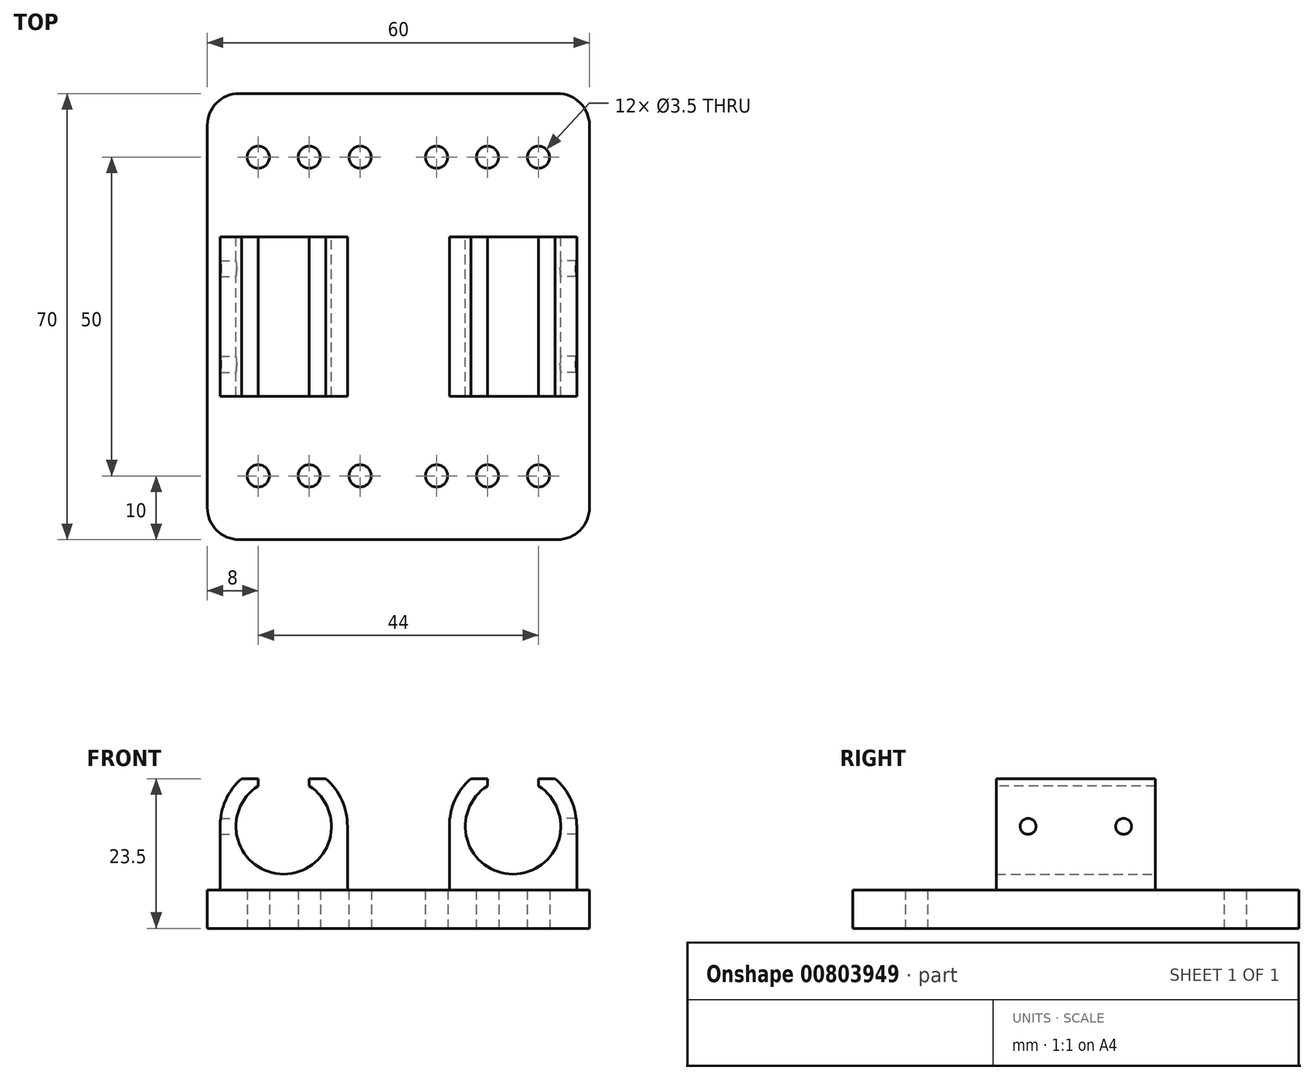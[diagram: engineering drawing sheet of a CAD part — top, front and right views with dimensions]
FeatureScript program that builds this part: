
annotation { "Feature Type Name" : "Feature", "Feature Type Description" : "" }
export const myFeature = defineFeature(function(context is Context, id is Id, definition is map)
    precondition{}
    {
        {
            var Q0;
            Q0=qCreatedBy(makeId("Top.planeOp"),FACE);
            var sketch = newSketch(context, id + "F0", { "sketchPlane" : qUnion([Q0])});
            skLineSegment(sketch, "E0.bottom", {"start": v(30, 35) * mm, "end": v(-30, 35) * mm});
            skLineSegment(sketch, "E0.top", {"start": v(30, -35) * mm, "end": v(-30, -35) * mm});
            skLineSegment(sketch, "E0.left", {"start": v(30, 35) * mm, "end": v(30, -35) * mm});
            skLineSegment(sketch, "E0.right", {"start": v(-30, 35) * mm, "end": v(-30, -35) * mm});
            skPoint(sketch, "E0.middle", {"position": v(0, 0) * mm});
            skLineSegment(sketch, "E1.bottom", {"start": v(-28, 12.5) * mm, "end": v(-8, 12.5) * mm});
            skLineSegment(sketch, "E1.top", {"start": v(-28, -12.5) * mm, "end": v(-8, -12.5) * mm});
            skLineSegment(sketch, "E1.left", {"start": v(-28, 12.5) * mm, "end": v(-28, -12.5) * mm});
            skLineSegment(sketch, "E1.right", {"start": v(-8, 12.5) * mm, "end": v(-8, -12.5) * mm});
            skPoint(sketch, "E1.middle", {"position": v(-18, 0) * mm});
            skLineSegment(sketch, "E2.bottom", {"start": v(8, 12.5) * mm, "end": v(28, 12.5) * mm});
            skLineSegment(sketch, "E2.top", {"start": v(8, -12.5) * mm, "end": v(28, -12.5) * mm});
            skLineSegment(sketch, "E2.left", {"start": v(8, 12.5) * mm, "end": v(8, -12.5) * mm});
            skLineSegment(sketch, "E2.right", {"start": v(28, 12.5) * mm, "end": v(28, -12.5) * mm});
            skPoint(sketch, "E2.middle", {"position": v(18, 0) * mm});
            skLineSegment(sketch, "E3", {"start": v(-30, -25) * mm, "end": v(30, -25) * mm});
            skPoint(sketch, "E4", {"position": v(22, -25) * mm});
            skPoint(sketch, "E5", {"position": v(6, -25) * mm});
            skPoint(sketch, "E6", {"position": v(-6, -25) * mm});
            skPoint(sketch, "E7", {"position": v(-22, -25) * mm});
            skPoint(sketch, "E8", {"position": v(-14, -25) * mm});
            skPoint(sketch, "E9", {"position": v(14, -25) * mm});
            skLineSegment(sketch, "E10", {"start": v(-30, 25) * mm, "end": v(30, 25) * mm});
            skPoint(sketch, "E11", {"position": v(-22, 25) * mm});
            skPoint(sketch, "E12", {"position": v(-14, 25) * mm});
            skPoint(sketch, "E13", {"position": v(-6, 25) * mm});
            skPoint(sketch, "E14", {"position": v(22, 25) * mm});
            skPoint(sketch, "E15", {"position": v(14, 25) * mm});
            skPoint(sketch, "E16", {"position": v(6, 25) * mm});
            skSolve(sketch);
        }
        {
            var Q0;
            Q0=makeQuery(id+"F0.imprint","IMPRINT",FACE,{"disambiguationData":[TD([[makeQuery(id+"F0.imprint","IMPRINT",EDGE,{"derivedFrom":sQuery(id+"F0.wireOp",EDGE,"E0.bottom")}),1.0]])]});
            var Q1;
            Q1=makeQuery(id+"F0.imprint","IMPRINT",FACE,{"disambiguationData":[TD([[makeQuery(id+"F0.imprint","IMPRINT",EDGE,{"derivedFrom":sQuery(id+"F0.wireOp",EDGE,"E1.bottom")}),-1.0]])]});
            var Q2;
            Q2=makeQuery(id+"F0.imprint","IMPRINT",FACE,{"disambiguationData":[TD([[makeQuery(id+"F0.imprint","IMPRINT",EDGE,{"derivedFrom":sQuery(id+"F0.wireOp",EDGE,"E2.bottom")}),-1.0]])]});
            var Q3;
            Q3=makeQuery(id+"F0.imprint","IMPRINT",FACE,{"disambiguationData":[TD([[makeQuery(id+"F0.imprint","IMPRINT",EDGE,{"derivedFrom":sQuery(id+"F0.wireOp",EDGE,"E1.bottom")}),1.0]])]});
            var Q4;
            {var subQ0=sQuery(id+"F0.wireOp",EDGE,"E0.top");Q4=makeQuery(id+"F0.imprint","IMPRINT",FACE,{"disambiguationData":[TD([[makeQuery(id+"F0.imprint","IMPRINT",EDGE,{"derivedFrom":subQ0}),-1.0]])]});}
            extrude(context, id + "F1", {"entities" : qUnion([Q0, Q1, Q2, Q3, Q4]), "oppositeDirection" : true, "depth" : 6 * mm, "offsetDistance" : 25 * mm});
        }
        {
            var Q0;
            Q0=makeQuery(id+"F0.imprint","IMPRINT",FACE,{"disambiguationData":[TD([[makeQuery(id+"F0.imprint","IMPRINT",EDGE,{"derivedFrom":sQuery(id+"F0.wireOp",EDGE,"E1.bottom")}),-1.0]])]});
            var Q1;
            Q1=makeQuery(id+"F0.imprint","IMPRINT",FACE,{"disambiguationData":[TD([[makeQuery(id+"F0.imprint","IMPRINT",EDGE,{"derivedFrom":sQuery(id+"F0.wireOp",EDGE,"E2.bottom")}),-1.0]])]});
            extrude(context, id + "F2", {"entities" : qUnion([Q0, Q1]), "operationType" : NewBodyOperationType.ADD, "depth" : 10 * mm, "offsetDistance" : 25 * mm});
        }
        {
            var Q0;
            Q0=makeQuery(id+"F2.opExtrude","SWEPT_FACE",FACE,{"disambiguationData":[OSD([sQuery(id+"F0.wireOp",EDGE,"E1.top")])]});
            var sketch = newSketch(context, id + "F3", { "sketchPlane" : qUnion([Q0])});
            skCircle(sketch, "E17", {"center": v(-18, 10) * mm, "radius": 10 * mm});
            skCircle(sketch, "E18", {"center": v(-18, 10) * mm, "radius": 7.5 * mm});
            skLineSegment(sketch, "E19.bottom", {"start": v(-11.39, 17.5) * mm, "end": v(-24.61, 17.5) * mm});
            skLineSegment(sketch, "E19.top", {"start": v(-11.39, 2.5) * mm, "end": v(-24.61, 2.5) * mm});
            skLineSegment(sketch, "E19.left", {"start": v(-11.39, 17.5) * mm, "end": v(-11.39, 2.5) * mm});
            skLineSegment(sketch, "E19.right", {"start": v(-24.61, 17.5) * mm, "end": v(-24.61, 2.5) * mm});
            skLineSegment(sketch, "E20.bottom", {"start": v(-22, 21.5) * mm, "end": v(-14, 21.5) * mm});
            skLineSegment(sketch, "E20.top", {"start": v(-22, 13.5) * mm, "end": v(-14, 13.5) * mm});
            skLineSegment(sketch, "E20.left", {"start": v(-22, 21.5) * mm, "end": v(-22, 13.5) * mm});
            skLineSegment(sketch, "E20.right", {"start": v(-14, 21.5) * mm, "end": v(-14, 13.5) * mm});
            skPoint(sketch, "E20.middle", {"position": v(-18, 17.5) * mm});
            skPoint(sketch, "E21", {"position": v(18, 10) * mm});
            skCircle(sketch, "E22", {"center": v(18, 10) * mm, "radius": 7.5 * mm});
            skSolve(sketch);
        }
        {
            var Q0;
            {var subQ4=sQuery(id+"F3.wireOp",EDGE,"E19.right");var subQ6=sQuery(id+"F3.wireOp",EDGE,"E18");var subQ7=makeQuery(id+"F3.imprint","INTERSECT",VERTEX,{"disambiguationData":[OD(0.0)],"derivedFrom":[subQ6,subQ4]});Q0=makeQuery(id+"F3.imprint","IMPRINT",FACE,{"disambiguationData":[TD([[makeQuery(id+"F3.imprint","IMPRINT",EDGE,{"disambiguationData":[TD([[subQ7,-1.0]])],"derivedFrom":subQ6}),-1.0]])]});}
            var Q1;
            {var subQ0=sQuery(id+"F3.wireOp",EDGE,"E20.left");var subQ1=sQuery(id+"F3.wireOp",EDGE,"E18");var subQ2=makeQuery(id+"F3.imprint","INTERSECT",VERTEX,{"derivedFrom":[subQ1,subQ0]});Q1=makeQuery(id+"F3.imprint","IMPRINT",FACE,{"disambiguationData":[TD([[makeQuery(id+"F3.imprint","IMPRINT",EDGE,{"disambiguationData":[TD([[subQ2,-1.0]])],"derivedFrom":subQ1}),-1.0]])]});}
            var Q2;
            {var subQ0=sQuery(id+"F3.wireOp",EDGE,"E19.left");var subQ1=sQuery(id+"F3.wireOp",EDGE,"E18");var subQ2=makeQuery(id+"F3.imprint","INTERSECT",VERTEX,{"disambiguationData":[OD(0.0)],"derivedFrom":[subQ1,subQ0]});Q2=makeQuery(id+"F3.imprint","IMPRINT",FACE,{"disambiguationData":[TD([[makeQuery(id+"F3.imprint","IMPRINT",EDGE,{"disambiguationData":[TD([[subQ2,-1.0]])],"derivedFrom":subQ1}),-1.0]])]});}
            var Q3;
            {var subQ4=sQuery(id+"F3.wireOp",EDGE,"E19.left");var subQ6=sQuery(id+"F3.wireOp",EDGE,"E18");var subQ7=makeQuery(id+"F3.imprint","INTERSECT",VERTEX,{"disambiguationData":[OD(0.0)],"derivedFrom":[subQ6,subQ4]});Q3=makeQuery(id+"F3.imprint","IMPRINT",FACE,{"disambiguationData":[TD([[makeQuery(id+"F3.imprint","IMPRINT",EDGE,{"disambiguationData":[TD([[subQ7,1.0]])],"derivedFrom":subQ6}),-1.0]])]});}
            extrude(context, id + "F4", {"entities" : qUnion([Q0, Q1, Q2, Q3]), "oppositeDirection" : true, "depth" : 25 * mm, "offsetDistance" : 25 * mm});
        }
        {
            var Q0;
            Q0=sQuery(id+"F3.wireOp",VERTEX,"E17.center");
            var Q1;
            Q1=makeQuery(id+"F1.opExtrude","SWEPT_BODY",BODY,{"disambiguationData":[OSD([sQuery(id+"F0.wireOp",EDGE,"E0.bottom"),sQuery(id+"F0.wireOp",EDGE,"E0.top"),sQuery(id+"F0.wireOp",EDGE,"E0.left"),sQuery(id+"F0.wireOp",EDGE,"E0.right")])]});
            hole(context, id + "F5", {"style" : HoleStyle.SIMPLE, "endStyle" : HoleEndStyle.THROUGH, "holeDiameter" : 15 * mm, "majorDiameter" : 5 * mm, "isTappedThrough" : true, "tappedDepth" : 12 * mm, "tapClearance" : 3, "locations" : qUnion([Q0]), "scope" : qUnion([Q1])});
        }
        {
            var Q0;
            Q0=makeQuery(id+"F1.opExtrude","SWEPT_BODY",BODY,{"disambiguationData":[OSD([sQuery(id+"F0.wireOp",EDGE,"E0.bottom"),sQuery(id+"F0.wireOp",EDGE,"E0.top"),sQuery(id+"F0.wireOp",EDGE,"E0.left"),sQuery(id+"F0.wireOp",EDGE,"E0.right")])]});
            var Q1;
            Q1=makeQuery(id+"F4.opExtrude","SWEPT_BODY",BODY,{"disambiguationData":[OSD([sQuery(id+"F0.wireOp",EDGE,"E1.top"),sQuery(id+"F3.wireOp",EDGE,"E17"),sQuery(id+"F3.wireOp",EDGE,"E18"),sQuery(id+"F3.wireOp",EDGE,"E19.bottom"),sQuery(id+"F3.wireOp",EDGE,"E20.right")])]});
            var Q2;
            Q2=makeQuery(id+"F4.opExtrude","SWEPT_BODY",BODY,{"disambiguationData":[OSD([sQuery(id+"F0.wireOp",EDGE,"E1.top"),sQuery(id+"F3.wireOp",EDGE,"E17"),sQuery(id+"F3.wireOp",EDGE,"E18"),sQuery(id+"F3.wireOp",EDGE,"E19.bottom"),sQuery(id+"F3.wireOp",EDGE,"E20.left")])]});
            booleanBodies(context, id + "F6", {"operationType" : BooleanOperationType.UNION, "tools" : qUnion([Q0, Q1, Q2])});
        }
        {
            var Q0;
            Q0=makeQuery(id+"F1.opExtrude","SWEPT_BODY",BODY,{"disambiguationData":[OSD([sQuery(id+"F0.wireOp",EDGE,"E0.bottom"),sQuery(id+"F0.wireOp",EDGE,"E0.top"),sQuery(id+"F0.wireOp",EDGE,"E0.left"),sQuery(id+"F0.wireOp",EDGE,"E0.right")])]});
            var Q1;
            Q1=qCreatedBy(makeId("Right.planeOp"),FACE);
            mirror(context, id + "F7", {"operationType" : NewBodyOperationType.ADD, "entities" : qUnion([Q0]), "mirrorPlane" : qUnion([Q1])});
        }
        {
            var Q0;
            {var subQ1=sQuery(id+"F3.wireOp",EDGE,"E18");var subQ5=sQuery(id+"F3.wireOp",EDGE,"E19.right");var subQ6=makeQuery(id+"F3.imprint","INTERSECT",VERTEX,{"disambiguationData":[OD(1.0)],"derivedFrom":[subQ1,subQ5]});Q0=makeQuery(id+"F3.imprint","IMPRINT",FACE,{"disambiguationData":[TD([[makeQuery(id+"F3.imprint","IMPRINT",EDGE,{"disambiguationData":[TD([[subQ6,-1.0]])],"derivedFrom":subQ1}),1.0]])]});}
            var Q1;
            {var subQ0=sQuery(id+"F3.wireOp",EDGE,"E19.right");var subQ1=sQuery(id+"F3.wireOp",EDGE,"E18");var subQ2=makeQuery(id+"F3.imprint","INTERSECT",VERTEX,{"disambiguationData":[OD(1.0)],"derivedFrom":[subQ1,subQ0]});Q1=makeQuery(id+"F3.imprint","IMPRINT",FACE,{"disambiguationData":[TD([[makeQuery(id+"F3.imprint","IMPRINT",EDGE,{"disambiguationData":[TD([[subQ2,1.0]])],"derivedFrom":subQ1}),1.0]])]});}
            var Q2;
            {var subQ0=sQuery(id+"F3.wireOp",EDGE,"E19.left");var subQ1=sQuery(id+"F3.wireOp",EDGE,"E18");var subQ2=makeQuery(id+"F3.imprint","INTERSECT",VERTEX,{"disambiguationData":[OD(1.0)],"derivedFrom":[subQ1,subQ0]});Q2=makeQuery(id+"F3.imprint","IMPRINT",FACE,{"disambiguationData":[TD([[makeQuery(id+"F3.imprint","IMPRINT",EDGE,{"disambiguationData":[TD([[subQ2,-1.0]])],"derivedFrom":subQ1}),1.0]])]});}
            extrude(context, id + "F8", {"entities" : qUnion([Q0, Q1, Q2]), "operationType" : NewBodyOperationType.REMOVE, "oppositeDirection" : true, "depth" : 25 * mm, "offsetDistance" : 25 * mm});
        }
        {
            var Q0;
            Q0=makeQuery(id+"F3.imprint","IMPRINT",FACE,{"disambiguationData":[TD([[makeQuery(id+"F3.imprint","IMPRINT",EDGE,{"derivedFrom":sQuery(id+"F3.wireOp",EDGE,"E22")}),1.0]])]});
            extrude(context, id + "F9", {"entities" : qUnion([Q0]), "operationType" : NewBodyOperationType.REMOVE, "oppositeDirection" : true, "depth" : 25 * mm, "offsetDistance" : 25 * mm});
        }
        {
            var Q0;
            Q0=makeQuery(id+"F1.opExtrude","SWEPT_EDGE",EDGE,{"disambiguationData":[OSD([sQuery(id+"F0.wireOp",EDGE,"E0.top"),sQuery(id+"F0.wireOp",EDGE,"E0.right")])]});
            var Q1;
            Q1=makeQuery(id+"F1.opExtrude","SWEPT_EDGE",EDGE,{"disambiguationData":[OSD([sQuery(id+"F0.wireOp",EDGE,"E0.top"),sQuery(id+"F0.wireOp",EDGE,"E0.left")])]});
            var Q2;
            Q2=makeQuery(id+"F1.opExtrude","SWEPT_EDGE",EDGE,{"disambiguationData":[OSD([sQuery(id+"F0.wireOp",EDGE,"E0.bottom"),sQuery(id+"F0.wireOp",EDGE,"E0.left")])]});
            var Q3;
            Q3=makeQuery(id+"F1.opExtrude","SWEPT_EDGE",EDGE,{"disambiguationData":[OSD([sQuery(id+"F0.wireOp",EDGE,"E0.bottom"),sQuery(id+"F0.wireOp",EDGE,"E0.right")])]});
            fillet(context, id + "F10", {"entities" : qUnion([Q0, Q1, Q2, Q3]), "radius" : 5 * mm, "tangentPropagation" : true, "allowEdgeOverflow" : false});
        }
        {
            var Q0;
            Q0=makeQuery(id+"F2.opExtrude","SWEPT_FACE",FACE,{"disambiguationData":[OSD([sQuery(id+"F0.wireOp",EDGE,"E2.right")])]});
            var sketch = newSketch(context, id + "F11", { "sketchPlane" : qUnion([Q0])});
            skPoint(sketch, "E23", {"position": v(-7.5, 10) * mm});
            skPoint(sketch, "E24", {"position": v(7.5, 10) * mm});
            skSolve(sketch);
        }
        {
            var Q0;
            Q0=sQuery(id+"F11.wireOp",VERTEX,"E23");
            var Q1;
            Q1=sQuery(id+"F11.wireOp",VERTEX,"E24");
            var Q2;
            Q2=makeQuery(id+"F1.opExtrude","SWEPT_BODY",BODY,{"disambiguationData":[OSD([sQuery(id+"F0.wireOp",EDGE,"E0.bottom"),sQuery(id+"F0.wireOp",EDGE,"E0.top"),sQuery(id+"F0.wireOp",EDGE,"E0.left"),sQuery(id+"F0.wireOp",EDGE,"E0.right")])]});
            hole(context, id + "F12", {"style" : HoleStyle.SIMPLE, "endStyle" : HoleEndStyle.BLIND, "holeDiameter" : 2.5 * mm, "majorDiameter" : 5 * mm, "holeDepth" : 10 * mm, "isTappedThrough" : true, "tappedDepth" : 12 * mm, "tapClearance" : 3, "locations" : qUnion([Q0, Q1]), "scope" : qUnion([Q2])});
        }
        {
            var Q0;
            Q0=makeQuery(id+"F2.opExtrude","SWEPT_FACE",FACE,{"disambiguationData":[OSD([sQuery(id+"F0.wireOp",EDGE,"E1.left")])]});
            var sketch = newSketch(context, id + "F13", { "sketchPlane" : qUnion([Q0])});
            skPoint(sketch, "E25", {"position": v(-7.5, 10) * mm});
            skPoint(sketch, "E26", {"position": v(7.5, 10) * mm});
            skSolve(sketch);
        }
        {
            var Q0;
            Q0=sQuery(id+"F13.wireOp",VERTEX,"E25");
            var Q1;
            Q1=sQuery(id+"F13.wireOp",VERTEX,"E26");
            var Q2;
            Q2=makeQuery(id+"F1.opExtrude","SWEPT_BODY",BODY,{"disambiguationData":[OSD([sQuery(id+"F0.wireOp",EDGE,"E0.bottom"),sQuery(id+"F0.wireOp",EDGE,"E0.top"),sQuery(id+"F0.wireOp",EDGE,"E0.left"),sQuery(id+"F0.wireOp",EDGE,"E0.right")])]});
            hole(context, id + "F14", {"style" : HoleStyle.SIMPLE, "endStyle" : HoleEndStyle.BLIND, "holeDiameter" : 2.5 * mm, "majorDiameter" : 5 * mm, "holeDepth" : 10 * mm, "isTappedThrough" : true, "tappedDepth" : 12 * mm, "tapClearance" : 3, "locations" : qUnion([Q0, Q1]), "scope" : qUnion([Q2])});
        }
        {
            var Q0;
            Q0=sQuery(id+"F0.wireOp",VERTEX,"E7");
            var Q1;
            Q1=sQuery(id+"F0.wireOp",VERTEX,"E8");
            var Q2;
            Q2=sQuery(id+"F0.wireOp",VERTEX,"E6");
            var Q3;
            Q3=sQuery(id+"F0.wireOp",VERTEX,"E5");
            var Q4;
            Q4=sQuery(id+"F0.wireOp",VERTEX,"E9");
            var Q5;
            Q5=sQuery(id+"F0.wireOp",VERTEX,"E4");
            var Q6;
            Q6=sQuery(id+"F0.wireOp",VERTEX,"E11");
            var Q7;
            Q7=sQuery(id+"F0.wireOp",VERTEX,"E12");
            var Q8;
            Q8=sQuery(id+"F0.wireOp",VERTEX,"E13");
            var Q9;
            Q9=sQuery(id+"F0.wireOp",VERTEX,"E16");
            var Q10;
            Q10=sQuery(id+"F0.wireOp",VERTEX,"E15");
            var Q11;
            Q11=sQuery(id+"F0.wireOp",VERTEX,"E14");
            var Q12;
            Q12=makeQuery(id+"F1.opExtrude","SWEPT_BODY",BODY,{"disambiguationData":[OSD([sQuery(id+"F0.wireOp",EDGE,"E0.bottom"),sQuery(id+"F0.wireOp",EDGE,"E0.top"),sQuery(id+"F0.wireOp",EDGE,"E0.left"),sQuery(id+"F0.wireOp",EDGE,"E0.right")])]});
            hole(context, id + "F15", {"style" : HoleStyle.SIMPLE, "endStyle" : HoleEndStyle.THROUGH, "holeDiameter" : 3.5 * mm, "majorDiameter" : 5 * mm, "isTappedThrough" : true, "tappedDepth" : 12 * mm, "tapClearance" : 3, "locations" : qUnion([Q0, Q1, Q2, Q3, Q4, Q5, Q6, Q7, Q8, Q9, Q10, Q11]), "scope" : qUnion([Q12])});
        }
    });
